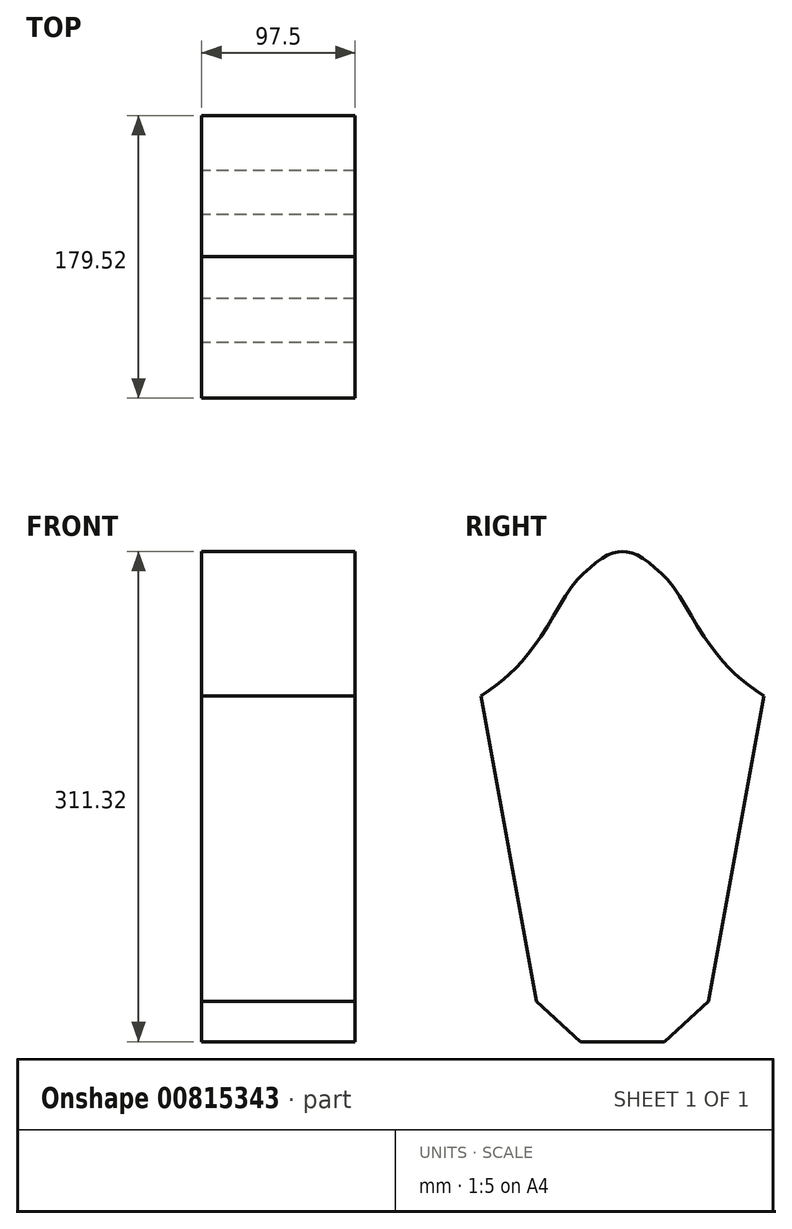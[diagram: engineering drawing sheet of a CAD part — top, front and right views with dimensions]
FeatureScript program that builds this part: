
annotation { "Feature Type Name" : "Feature", "Feature Type Description" : "" }
export const myFeature = defineFeature(function(context is Context, id is Id, definition is map)
    precondition{}
    {
        {
            var Q0;
            Q0=qCreatedBy(makeId("Right.planeOp"),FACE);
            var sketch = newSketch(context, id + "F0", { "sketchPlane" : qUnion([Q0])});
            skFitSpline(sketch, "E0", {"points": [v(0, 116.17) * mm, v(3.06, 115.78) * mm, v(7.67, 113.9) * mm, v(14.22, 108.94) * mm, v(22.25, 100.28) * mm, v(32.3, 83.46) * mm, v(42.34, 70.02) * mm, v(50.07, 62.3) * mm, v(59.84, 54.97) * mm], "startDerivative": vector(42.97, -3.15) * mm, "endDerivative": vector(75.08, -53.22) * mm});
            skLineSegment(sketch, "E1", {"start": v(59.84, 54.97) * mm, "end": v(36.42, -74.25) * mm});
            skLineSegment(sketch, "E2", {"start": v(36.42, -74.25) * mm, "end": v(17.78, -91.38) * mm});
            skLineSegment(sketch, "E3", {"start": v(17.78, -91.38) * mm, "end": v(0, -91.38) * mm});
            skLineSegment(sketch, "E4.MirrorCS", {"start": v(-59.84, 54.97) * mm, "end": v(-36.42, -74.25) * mm});
            skLineSegment(sketch, "E5.MirrorCS", {"start": v(-36.42, -74.25) * mm, "end": v(-17.78, -91.38) * mm});
            skLineSegment(sketch, "E6.MirrorCS", {"start": v(-17.78, -91.38) * mm, "end": v(0, -91.38) * mm});
            skFitSpline(sketch, "E7.MirrorCS", {"points": [v(0, 116.17) * mm, v(-3.06, 115.78) * mm, v(-7.67, 113.9) * mm, v(-14.22, 108.94) * mm, v(-22.25, 100.28) * mm, v(-32.3, 83.46) * mm, v(-42.34, 70.02) * mm, v(-50.07, 62.3) * mm, v(-59.84, 54.97) * mm], "startDerivative": vector(-42.97, -3.15) * mm, "endDerivative": vector(-75.08, -53.22) * mm});
            skSolve(sketch);
        }
        {
            var Q0;
            Q0=makeQuery(id+"F0.imprint","IMPRINT",FACE,{"disambiguationData":[TD([[makeQuery(id+"F0.imprint","IMPRINT",EDGE,{"derivedFrom":sQuery(id+"F0.wireOp",EDGE,"E0")}),-1.0]])]});
            extrude(context, id + "F1", {"entities" : qUnion([Q0]), "depth" : 65 * mm, "offsetDistance" : 25 * mm});
        }
        {
            var Q0;
            Q0=makeQuery(id+"F1.opExtrude","SWEPT_BODY",BODY,{"disambiguationData":[OSD([sQuery(id+"F0.wireOp",EDGE,"E0"),sQuery(id+"F0.wireOp",EDGE,"E1"),sQuery(id+"F0.wireOp",EDGE,"E2"),sQuery(id+"F0.wireOp",EDGE,"E3"),sQuery(id+"F0.wireOp",EDGE,"E4.MirrorCS"),sQuery(id+"F0.wireOp",EDGE,"E5.MirrorCS"),sQuery(id+"F0.wireOp",EDGE,"E6.MirrorCS"),sQuery(id+"F0.wireOp",EDGE,"E7.MirrorCS")])]});
            var Q1;
            Q1=qCreatedBy(makeId("Origin.pointOp"),VERTEX);
            transform(context, id + "F2", {"entities" : qUnion([Q0]), "transformType" : TransformType.SCALE_UNIFORMLY, "scale" : 1.5, "scalePoint" : qUnion([Q1]), "makeCopy" : false});
        }
        {
            var Q0;
            Q0=qCreatedBy(makeId("Front.planeOp"),FACE);
            cPlane(context, id + "F3", {"entities" : qUnion([Q0]), "cplaneType" : CPlaneType.OFFSET, "offset" : 75 * mm, "width" : 150 * mm, "height" : 150 * mm});
        }
    });
